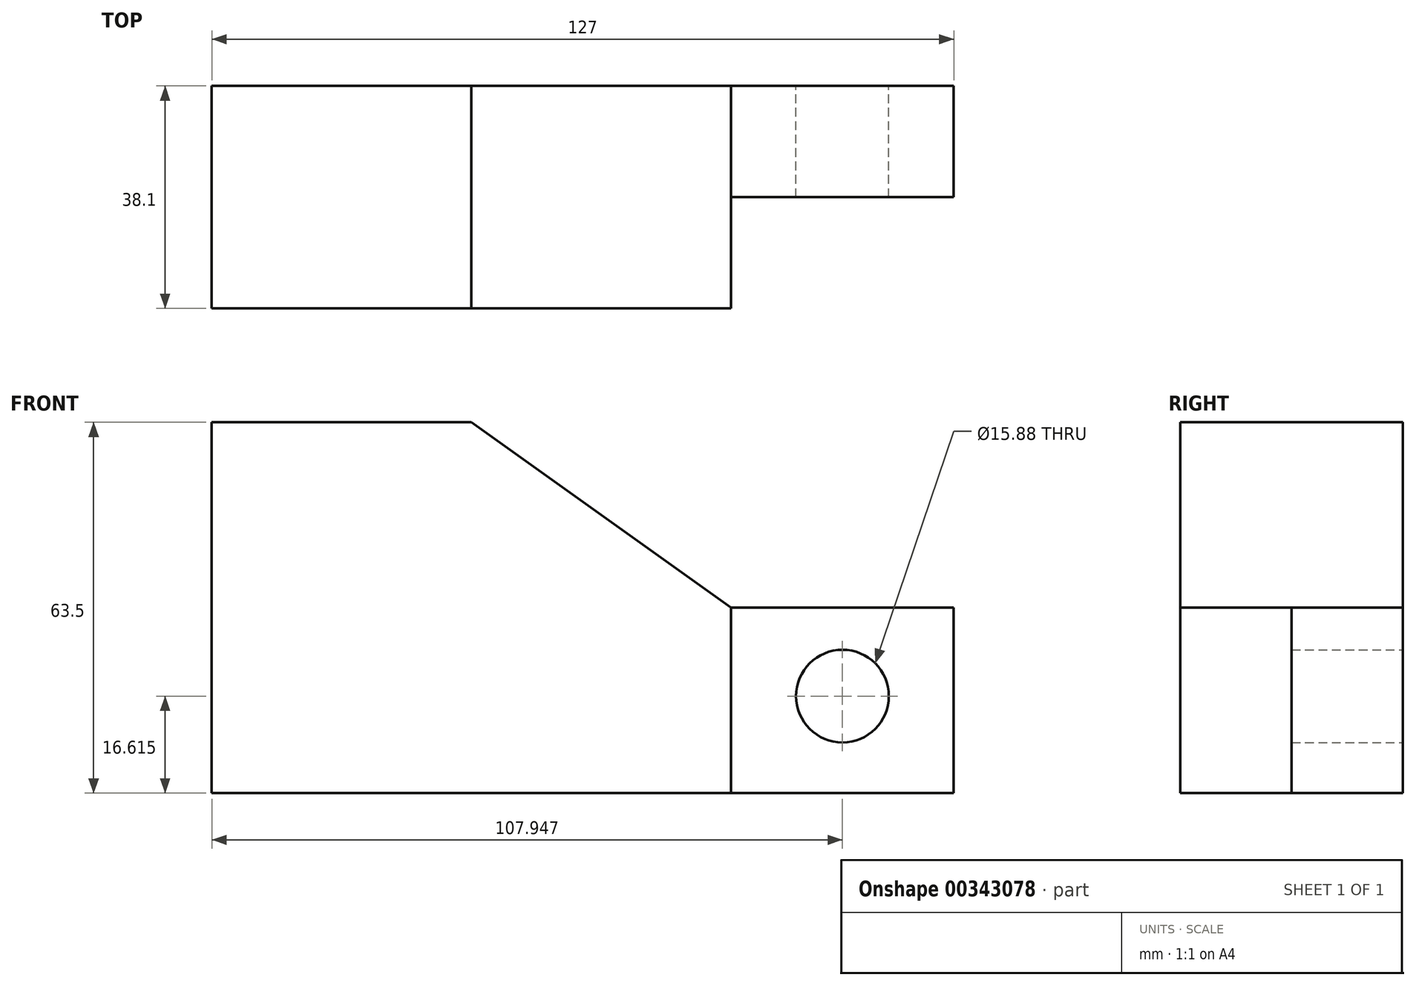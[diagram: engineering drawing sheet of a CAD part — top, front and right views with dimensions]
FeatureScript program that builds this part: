
annotation { "Feature Type Name" : "Feature", "Feature Type Description" : "" }
export const myFeature = defineFeature(function(context is Context, id is Id, definition is map)
    precondition{}
    {
        {
            var Q0;
            Q0=qCreatedBy(makeId("Front.planeOp"),FACE);
            var sketch = newSketch(context, id + "F0", { "sketchPlane" : qUnion([Q0])});
            skLineSegment(sketch, "E0", {"start": v(-53.92, -40.37) * mm, "end": v(73.08, -40.37) * mm});
            skLineSegment(sketch, "E1", {"start": v(73.08, -40.37) * mm, "end": v(-53.92, -40.37) * mm});
            skLineSegment(sketch, "E2", {"start": v(-53.92, -40.37) * mm, "end": v(-53.92, 23.13) * mm});
            skLineSegment(sketch, "E3", {"start": v(73.08, -40.37) * mm, "end": v(73.08, -8.62) * mm});
            skLineSegment(sketch, "E4", {"start": v(34.98, -8.62) * mm, "end": v(34.98, -40.37) * mm});
            skLineSegment(sketch, "E5", {"start": v(-53.92, 23.13) * mm, "end": v(-9.47, 23.13) * mm});
            skLineSegment(sketch, "E6", {"start": v(-9.47, 23.13) * mm, "end": v(34.98, -8.62) * mm});
            skLineSegment(sketch, "E7", {"start": v(34.98, -8.62) * mm, "end": v(54.03, -8.62) * mm});
            skLineSegment(sketch, "E8", {"start": v(54.03, -8.62) * mm, "end": v(73.08, -8.62) * mm});
            skCircle(sketch, "E9", {"center": v(54.03, -23.76) * mm, "radius": 7.94 * mm});
            skSolve(sketch);
        }
        {
            var Q0;
            {var subQ1=sQuery(id+"F0.wireOp",EDGE,"E2");Q0=makeQuery(id+"F0.imprint","IMPRINT",FACE,{"disambiguationData":[TD([[makeQuery(id+"F0.imprint","IMPRINT",EDGE,{"derivedFrom":subQ1}),-1.0]])]});}
            extrude(context, id + "F1", {"entities" : qUnion([Q0]), "depth" : 38.1 * mm});
        }
        {
            var Q0;
            {var subQ1=sQuery(id+"F0.wireOp",EDGE,"E3");Q0=makeQuery(id+"F0.imprint","IMPRINT",FACE,{"disambiguationData":[TD([[makeQuery(id+"F0.imprint","IMPRINT",EDGE,{"derivedFrom":subQ1}),1.0]])]});}
            extrude(context, id + "F2", {"entities" : qUnion([Q0]), "operationType" : NewBodyOperationType.ADD, "depth" : 19.05 * mm});
        }
    });
